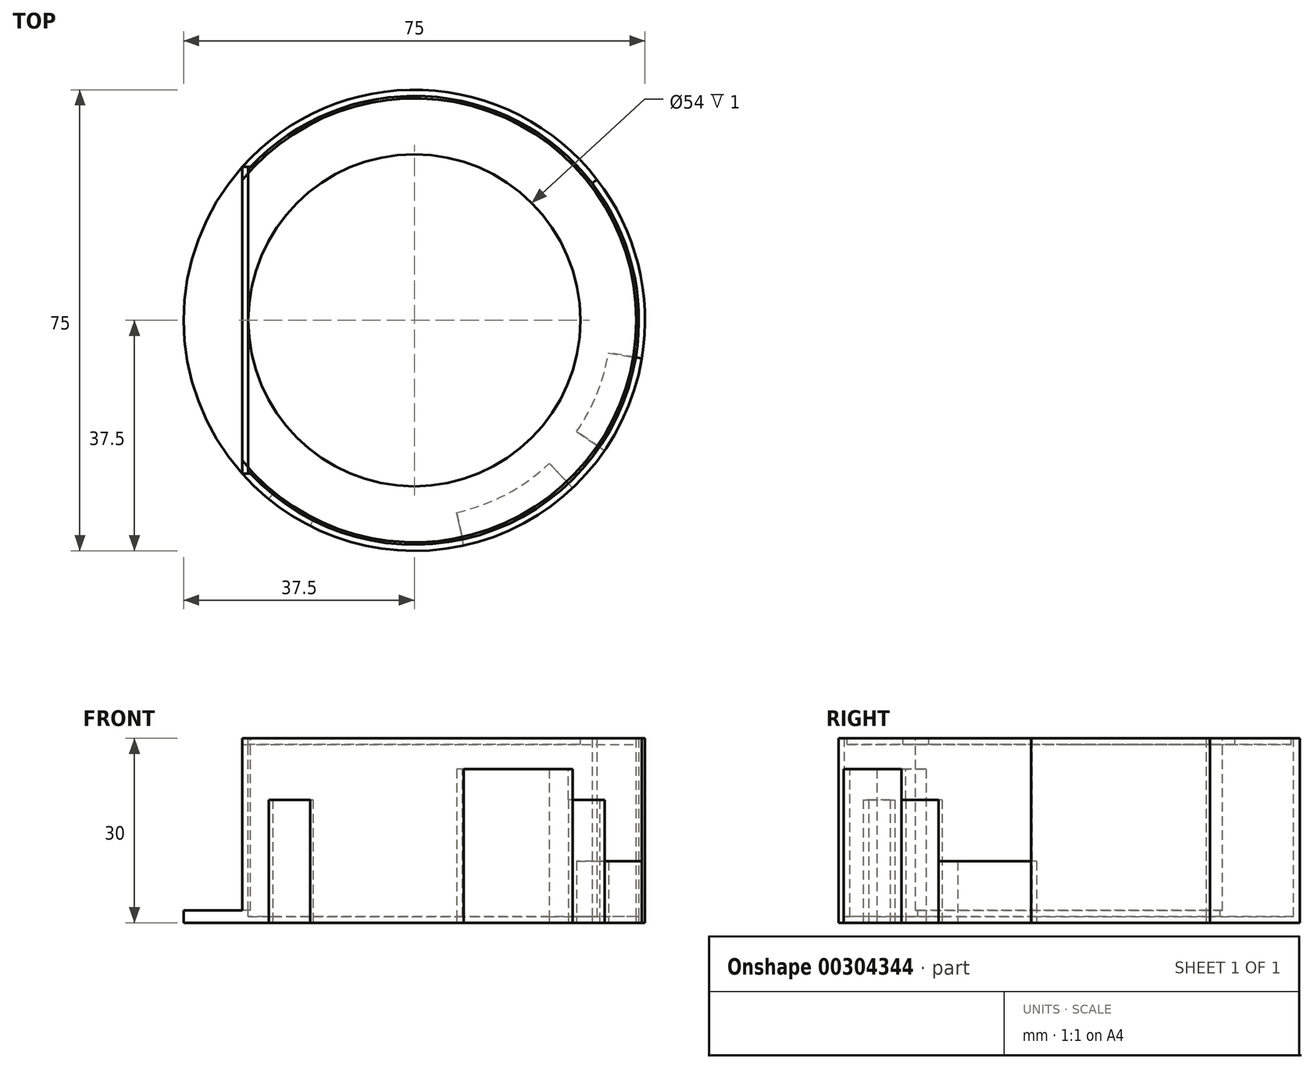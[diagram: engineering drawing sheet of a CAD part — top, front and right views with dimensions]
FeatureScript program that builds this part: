
annotation { "Feature Type Name" : "Feature", "Feature Type Description" : "" }
export const myFeature = defineFeature(function(context is Context, id is Id, definition is map)
    precondition{}
    {
        {
            var Q0;
            Q0=qCreatedBy(makeId("Top.planeOp"),FACE);
            var sketch = newSketch(context, id + "F0", { "sketchPlane" : qUnion([Q0])});
            skCircle(sketch, "E0", {"center": v(0, 0) * mm, "radius": 37.5 * mm});
            skSolve(sketch);
        }
        {
            var Q0;
            Q0=makeQuery(id+"F0.imprint","IMPRINT",FACE,{"disambiguationData":[TD([[makeQuery(id+"F0.imprint","IMPRINT",EDGE,{"derivedFrom":sQuery(id+"F0.wireOp",EDGE,"E0")}),1.0]])]});
            extrude(context, id + "F1", {"entities" : qUnion([Q0]), "oppositeDirection" : true, "depth" : 30 * mm});
        }
        {
            var Q0;
            Q0=qSketchRegion(id+"F0",true);
            var sketch = newSketch(context, id + "F2", { "sketchPlane" : qUnion([Q0])});
            skLineSegment(sketch, "E1", {"start": v(-28, 24.94) * mm, "end": v(-28, -24.94) * mm});
            skSolve(sketch);
        }
        {
            var Q0;
            {var subQ0=sQuery(id+"F2.wireOp",EDGE,"E1");Q0=makeQuery(id+"F2.imprint","IMPRINT",FACE,{"disambiguationData":[TD([[makeQuery(id+"F2.imprint","IMPRINT",EDGE,{"derivedFrom":subQ0}),-1.0]])]});}
            extrude(context, id + "F3", {"entities" : qUnion([Q0]), "operationType" : NewBodyOperationType.REMOVE, "oppositeDirection" : true, "depth" : 28 * mm});
        }
        {
            var Q0;
            {var subQ0=sQuery(id+"F2.wireOp",EDGE,"E1");Q0=makeQuery(id+"F2.imprint","IMPRINT",FACE,{"disambiguationData":[TD([[makeQuery(id+"F2.imprint","IMPRINT",EDGE,{"derivedFrom":subQ0}),1.0]])]});}
            var sketch = newSketch(context, id + "F4", { "sketchPlane" : qUnion([Q0])});
            skCircle(sketch, "E2", {"center": v(0, 0) * mm, "radius": 27 * mm});
            skArc(sketch, "E3", {"start": v(-28, 22.79) * mm, "mid": v(36.1, 0) * mm, "end": v(-28, -22.79) * mm});
            skLineSegment(sketch, "E4", {"start": v(-28, -22.79) * mm, "end": v(-28, 22.79) * mm});
            skSolve(sketch);
        }
        {
            var Q0;
            {var subQ0=sQuery(id+"F2.wireOp",EDGE,"E1");Q0=makeQuery(id+"F2.imprint","IMPRINT",FACE,{"disambiguationData":[TD([[makeQuery(id+"F2.imprint","IMPRINT",EDGE,{"derivedFrom":subQ0}),1.0]])]});}
            var sketch = newSketch(context, id + "F5", { "sketchPlane" : qUnion([Q0])});
            skArc(sketch, "E5", {"start": v(-23.66, -29.1) * mm, "mid": v(-20.43, -31.45) * mm, "end": v(-16.95, -33.45) * mm});
            skSolve(sketch);
        }
        {
            var Q0;
            Q0=makeQuery(id+"F1.opExtrude","CAP_FACE",FACE,{"disambiguationData":[OSD([sQuery(id+"F0.wireOp",EDGE,"E0")])],"isStart":false});
            var sketch = newSketch(context, id + "F6", { "sketchPlane" : qUnion([Q0])});
            skArc(sketch, "E6", {"start": v(-23.66, 29.1) * mm, "mid": v(-20.43, 31.45) * mm, "end": v(-16.95, 33.45) * mm});
            skArc(sketch, "E7", {"start": v(-23.03, 28.32) * mm, "mid": v(-19.88, 30.61) * mm, "end": v(-16.5, 32.56) * mm});
            skLineSegment(sketch, "E8", {"start": v(-23.66, 29.1) * mm, "end": v(-23.03, 28.32) * mm});
            skLineSegment(sketch, "E9", {"start": v(-16.95, 33.45) * mm, "end": v(-16.5, 32.56) * mm});
            skLineSegment(sketch, "E10", {"start": v(0, 0) * mm, "end": v(-23.66, 29.1) * mm, "construction": true});
            skLineSegment(sketch, "E11", {"start": v(-16.95, 33.45) * mm, "end": v(0, 0) * mm, "construction": true});
            skSolve(sketch);
        }
        {
            var Q0;
            Q0=makeQuery(id+"F1.opExtrude","CAP_FACE",FACE,{"disambiguationData":[OSD([sQuery(id+"F0.wireOp",EDGE,"E0")])],"isStart":false});
            var sketch = newSketch(context, id + "F7", { "sketchPlane" : qUnion([Q0])});
            skArc(sketch, "E12", {"start": v(8.05, 36.63) * mm, "mid": v(17.52, 33.15) * mm, "end": v(25.73, 27.28) * mm});
            skArc(sketch, "E13", {"start": v(25.73, 27.28) * mm, "mid": v(28.5, 24.38) * mm, "end": v(30.93, 21.2) * mm});
            skArc(sketch, "E14", {"start": v(30.93, 21.2) * mm, "mid": v(34.78, 14.03) * mm, "end": v(36.98, 6.2) * mm});
            skArc(sketch, "E15", {"start": v(36.98, 6.2) * mm, "mid": v(36.38, -9.1) * mm, "end": v(29.7, -22.9) * mm});
            skLineSegment(sketch, "E16", {"start": v(0, 0) * mm, "end": v(29.7, -22.9) * mm, "construction": true});
            skLineSegment(sketch, "E17", {"start": v(36.98, 6.2) * mm, "end": v(0, 0) * mm, "construction": true});
            skLineSegment(sketch, "E18", {"start": v(30.93, 21.2) * mm, "end": v(0, 0) * mm, "construction": true});
            skLineSegment(sketch, "E19", {"start": v(25.73, 27.28) * mm, "end": v(0, 0) * mm, "construction": true});
            skLineSegment(sketch, "E20", {"start": v(0, 0) * mm, "end": v(8.05, 36.63) * mm, "construction": true});
            skArc(sketch, "E21", {"start": v(6.87, 31.25) * mm, "mid": v(14.95, 28.3) * mm, "end": v(21.96, 23.28) * mm});
            skArc(sketch, "E22", {"start": v(31.56, 5.3) * mm, "mid": v(29.67, 11.98) * mm, "end": v(26.4, 18.1) * mm});
            skLineSegment(sketch, "E23", {"start": v(25.73, 27.28) * mm, "end": v(21.96, 23.28) * mm});
            skLineSegment(sketch, "E24", {"start": v(8.05, 36.63) * mm, "end": v(6.87, 31.25) * mm});
            skLineSegment(sketch, "E25", {"start": v(26.4, 18.1) * mm, "end": v(30.93, 21.2) * mm});
            skLineSegment(sketch, "E26", {"start": v(31.56, 5.3) * mm, "end": v(36.98, 6.2) * mm});
            skArc(sketch, "E27", {"start": v(25.04, 26.55) * mm, "mid": v(27.73, 23.73) * mm, "end": v(30.1, 20.64) * mm});
            skLineSegment(sketch, "E28", {"start": v(30.93, 21.2) * mm, "end": v(30.1, 20.64) * mm});
            skLineSegment(sketch, "E29", {"start": v(25.73, 27.28) * mm, "end": v(25.04, 26.55) * mm});
            skArc(sketch, "E30", {"start": v(36, 6.04) * mm, "mid": v(35.4, -8.86) * mm, "end": v(28.9, -22.29) * mm});
            skLineSegment(sketch, "E31", {"start": v(29.7, -22.9) * mm, "end": v(28.9, -22.29) * mm});
            skSolve(sketch);
        }
        {
            var Q0;
            Q0=makeQuery(id+"F1.opExtrude","CAP_FACE",FACE,{"disambiguationData":[OSD([sQuery(id+"F0.wireOp",EDGE,"E0")])],"isStart":true});
            shell(context, id + "F8", {"entities" : qUnion([Q0]), "thickness" : 1 * mm});
        }
        {
            var Q0;
            Q0 = qSketchRegion(id + "F6", true);
            extrude(context, id + "F9", {"entities" : qUnion([Q0]), "operationType" : NewBodyOperationType.REMOVE, "oppositeDirection" : true, "depth" : 20 * mm});
        }
        {
            var Q0;
            Q0 = qSketchRegion(id + "F6", true);
            extrude(context, id + "F10", {"entities" : qUnion([Q0]), "oppositeDirection" : true, "depth" : 20 * mm});
        }
        {
            var Q0;
            Q0=makeQuery(id+"F7.imprint","IMPRINT",FACE,{"disambiguationData":[TD([[makeQuery(id+"F7.imprint","IMPRINT",EDGE,{"derivedFrom":sQuery(id+"F7.wireOp",EDGE,"E12")}),-1.0]])]});
            extrude(context, id + "F11", {"entities" : qUnion([Q0]), "operationType" : NewBodyOperationType.REMOVE, "oppositeDirection" : true, "depth" : 25 * mm});
        }
        {
            var Q0;
            Q0=makeQuery(id+"F7.imprint","IMPRINT",FACE,{"disambiguationData":[TD([[makeQuery(id+"F7.imprint","IMPRINT",EDGE,{"derivedFrom":sQuery(id+"F7.wireOp",EDGE,"E12")}),-1.0]])]});
            extrude(context, id + "F12", {"entities" : qUnion([Q0]), "oppositeDirection" : true, "depth" : 25 * mm});
        }
        {
            var Q0;
            {var subQ3=sQuery(id+"F7.wireOp",EDGE,"E14");Q0=makeQuery(id+"F7.imprint","IMPRINT",FACE,{"disambiguationData":[TD([[makeQuery(id+"F7.imprint","IMPRINT",EDGE,{"derivedFrom":subQ3}),-1.0]])]});}
            extrude(context, id + "F13", {"entities" : qUnion([Q0]), "operationType" : NewBodyOperationType.REMOVE, "oppositeDirection" : true, "depth" : 10 * mm});
        }
        {
            var Q0;
            {var subQ3=sQuery(id+"F7.wireOp",EDGE,"E14");Q0=makeQuery(id+"F7.imprint","IMPRINT",FACE,{"disambiguationData":[TD([[makeQuery(id+"F7.imprint","IMPRINT",EDGE,{"derivedFrom":subQ3}),-1.0]])]});}
            extrude(context, id + "F14", {"entities" : qUnion([Q0]), "oppositeDirection" : true, "depth" : 10 * mm});
        }
        {
            var Q0;
            {var subQ0=sQuery(id+"F7.wireOp",EDGE,"E15");Q0=makeQuery(id+"F7.imprint","IMPRINT",FACE,{"disambiguationData":[TD([[makeQuery(id+"F7.imprint","IMPRINT",EDGE,{"derivedFrom":subQ0}),-1.0]])]});}
            extrude(context, id + "F15", {"entities" : qUnion([Q0]), "operationType" : NewBodyOperationType.REMOVE, "oppositeDirection" : true, "depth" : 30 * mm});
        }
        {
            var Q0;
            {var subQ0=sQuery(id+"F7.wireOp",EDGE,"E15");Q0=makeQuery(id+"F7.imprint","IMPRINT",FACE,{"disambiguationData":[TD([[makeQuery(id+"F7.imprint","IMPRINT",EDGE,{"derivedFrom":subQ0}),-1.0]])]});}
            extrude(context, id + "F16", {"entities" : qUnion([Q0]), "oppositeDirection" : true, "depth" : 30 * mm});
        }
        {
            var Q0;
            Q0=makeQuery(id+"F7.imprint","IMPRINT",FACE,{"disambiguationData":[TD([[makeQuery(id+"F7.imprint","IMPRINT",EDGE,{"derivedFrom":sQuery(id+"F7.wireOp",EDGE,"E13")}),-1.0]])]});
            extrude(context, id + "F17", {"entities" : qUnion([Q0]), "operationType" : NewBodyOperationType.REMOVE, "oppositeDirection" : true, "depth" : 20 * mm});
        }
        {
            var Q0;
            Q0=makeQuery(id+"F7.imprint","IMPRINT",FACE,{"disambiguationData":[TD([[makeQuery(id+"F7.imprint","IMPRINT",EDGE,{"derivedFrom":sQuery(id+"F7.wireOp",EDGE,"E13")}),-1.0]])]});
            extrude(context, id + "F18", {"entities" : qUnion([Q0]), "oppositeDirection" : true, "depth" : 20 * mm});
        }
        {
            var Q0;
            Q0=makeQuery(id+"F3.boolean.opBoolean","COPY",FACE,{"derivedFrom":makeQuery(id+"F3.opExtrude","SWEPT_FACE",FACE,{"disambiguationData":[OSD([sQuery(id+"F2.wireOp",EDGE,"E1")])]})});
            var sketch = newSketch(context, id + "F19", { "sketchPlane" : qUnion([Q0])});
            skLineSegment(sketch, "E32", {"start": v(24.94, -28) * mm, "end": v(24.94, 0) * mm});
            skLineSegment(sketch, "E33", {"start": v(24.94, 0) * mm, "end": v(-24.94, 0) * mm});
            skLineSegment(sketch, "E34", {"start": v(-24.94, 0) * mm, "end": v(-24.94, -28) * mm});
            skLineSegment(sketch, "E35", {"start": v(-24.94, -28) * mm, "end": v(24.94, -28) * mm});
            skSolve(sketch);
        }
        {
            var Q0;
            Q0=makeQuery(id+"F19.imprint","IMPRINT",FACE,{"disambiguationData":[TD([[makeQuery(id+"F19.imprint","IMPRINT",EDGE,{"derivedFrom":sQuery(id+"F19.wireOp",EDGE,"E32")}),1.0]])]});
            extrude(context, id + "F20", {"entities" : qUnion([Q0]), "operationType" : NewBodyOperationType.REMOVE, "endBound" : BoundingType.UP_TO_NEXT, "oppositeDirection" : true, "depth" : 25 * mm});
        }
        {
            var Q0;
            Q0=makeQuery(id+"F19.imprint","IMPRINT",FACE,{"disambiguationData":[TD([[makeQuery(id+"F19.imprint","IMPRINT",EDGE,{"derivedFrom":sQuery(id+"F19.wireOp",EDGE,"E32")}),1.0]])]});
            extrude(context, id + "F21", {"entities" : qUnion([Q0]), "oppositeDirection" : true, "depth" : 1 * mm});
        }
        {
            var Q0;
            Q0=makeQuery(id+"F4.imprint","IMPRINT",FACE,{"disambiguationData":[TD([[makeQuery(id+"F4.imprint","IMPRINT",EDGE,{"derivedFrom":sQuery(id+"F4.wireOp",EDGE,"E2")}),-1.0]])]});
            extrude(context, id + "F22", {"entities" : qUnion([Q0]), "oppositeDirection" : true, "depth" : 1 * mm});
        }
    });
